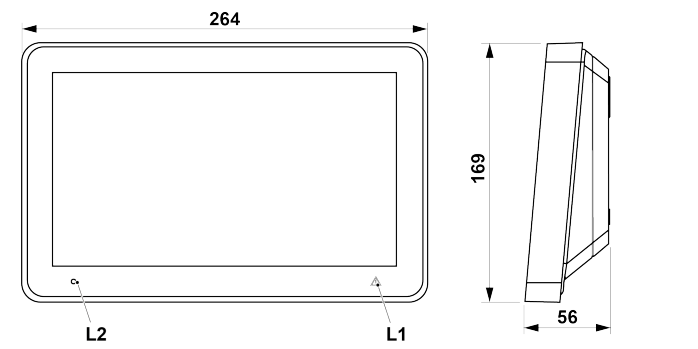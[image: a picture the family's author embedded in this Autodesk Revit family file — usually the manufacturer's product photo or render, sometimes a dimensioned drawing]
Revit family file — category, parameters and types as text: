
# Revit family: 5054_Display Unit
name_source: partatom
category: Fire Alarm Devices
units: mm (PartAtom-declared; Revit-internal decimal feet)

## family parameters
Cut with Voids When Loaded = No
Host = Face
Maintain Annotation Orientation = No
OmniClass Number = 23.85.30.21
OmniClass Title = Environmental Detection/Registration
Part Type = Normal
Room Calculation Point = No
Round Connector Dimension = Use Diameter
Shared = No

## types (1)
- 5054
    Ambient Humidity = Maximum 93 % RH
    Ambient Temperature Operating = -5 to +40 °C
    Ambient Temperature Storage = -30 to +80 °C
    Buzzer = Yes
    Connection = RS485 (Redundancy)
    Current Active_12 VDC = 350 mA
    Current Active_24 VDC = 180 mA
    Current Quiescent_12 VDC = 80 mA
    Current Quiescent_24 VDC = 45 mA
    Default Elevation = 0 mm  [stored 0 ft]
    Depth (mm) = 56 mm  [stored 0.183727 ft]
    Description = Display unit 5054
    Display Size = 10.1 inch
    Height (mm) = 169 mm  [stored 0.554462 ft]
    Ingress Protection Rating = IP30
    Manufacturer = Panasonic
    Max_Wire Size = Ø 1.85 mm (2.08 mm²)
    Min_Wire Size = Ø 0.6 mm (0.3 mm²)
    Model = 5054
    Omniclass Code = 23.85.30.21.11.11.11
    Omniclass Description = Smoke Detectors
    Product Material = PC/ABS Polyblend 65FS_Light grey (NCS S 1500-N)
    Resolution = 1024x600 RGB
    Selectable Function = Presentation unit, fire brigade panel, alert annunciation unit, general control panel
    Short Circuit Isolator = No
    Tested and Approved = Design to comply with EN54-2 in applicable parts
    Type Comments = The display unit 5054 consists of a colour touch display and has multi language support. It is intended to be used for fire alarms and information in the fire alarm system. Up to 30 units can be connected to one EBL Control unit. Up to 1200 meters to the unit farthest away. Highest security, fully redundant 24V and RS485 connection
    URL = https://www.panasonic-fire-security.com
    Uniclass 2015 Code = Pr_75_80_30_27
    Uniclass 2015 Description = Fire and smoke detector bases
    Uniformat 2010  Code = D7050
    Uniformat 2010 Description = Detection and Alarm
    Version = RVT20
    Voltage Allowed = 12 – 30 VDC
    Voltage Normal = 24 VDC
    Weight = 1400 g
    Width (mm) = 264 mm  [stored 0.866142 ft]

note: [stored X ft] marks values corroborated as IEEE doubles in the binary element streams (Revit-internal decimal feet)

## geometry (parser evidence)
native form markers: Blend x2, Sweep x6
no freeform markers — native parametric forms only
